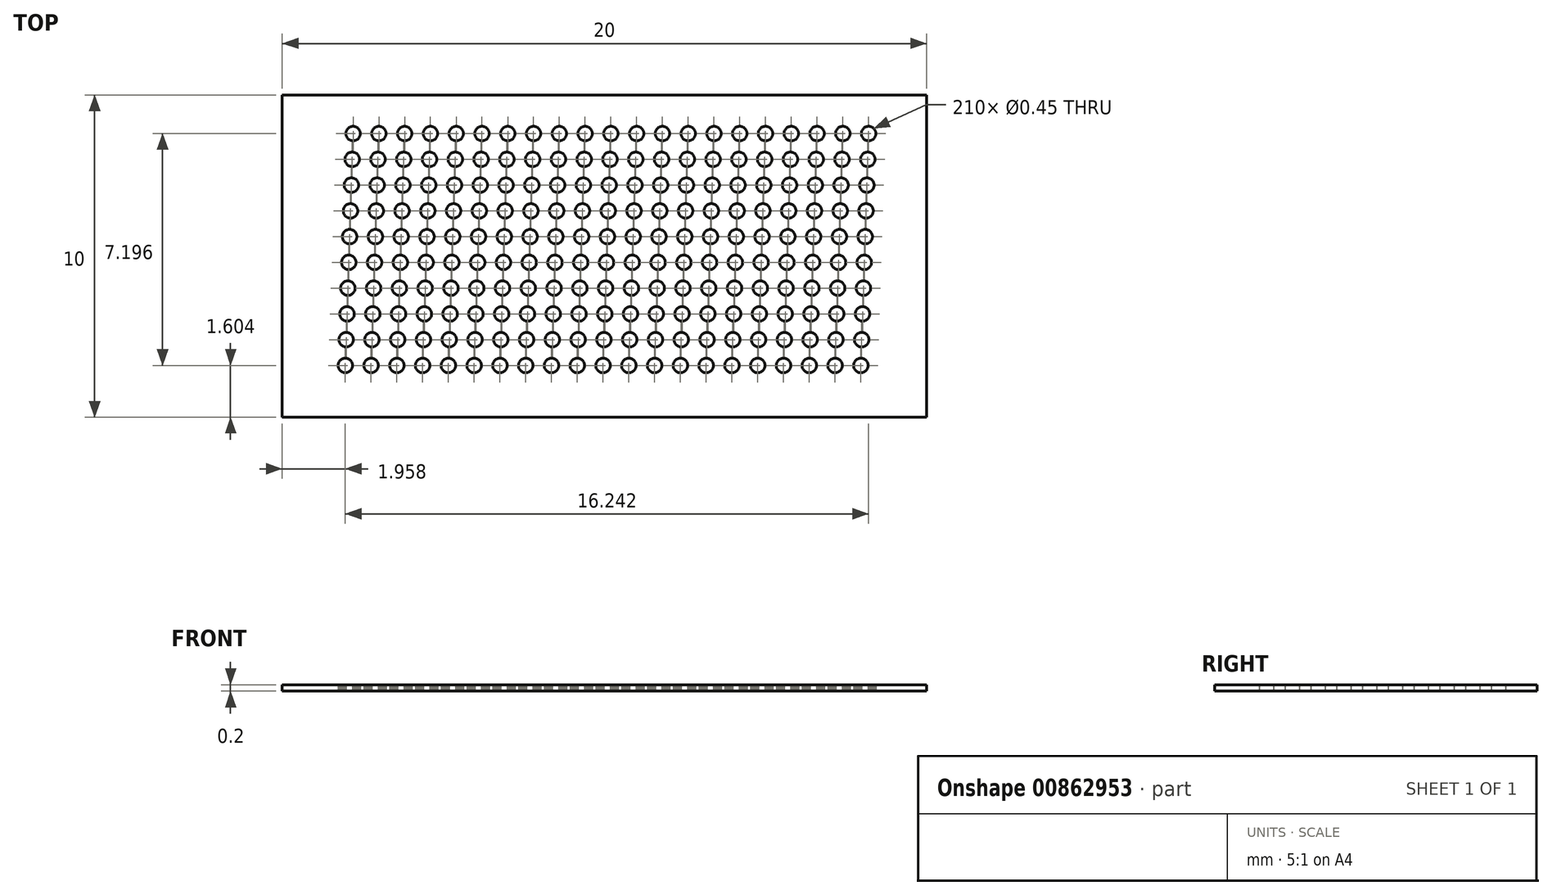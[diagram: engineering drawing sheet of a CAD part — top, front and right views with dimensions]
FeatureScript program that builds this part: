
annotation { "Feature Type Name" : "Feature", "Feature Type Description" : "" }
export const myFeature = defineFeature(function(context is Context, id is Id, definition is map)
    precondition{}
    {
        {
            var Q0;
            Q0=qCreatedBy(makeId("Top.planeOp"),FACE);
            var sketch = newSketch(context, id + "F0", { "sketchPlane" : qUnion([Q0])});
            skLineSegment(sketch, "E0.bottom", {"start": v(0, 0) * mm, "end": v(20, 0) * mm});
            skLineSegment(sketch, "E0.top", {"start": v(0, -10) * mm, "end": v(20, -10) * mm});
            skLineSegment(sketch, "E0.left", {"start": v(0, 0) * mm, "end": v(0, -10) * mm});
            skLineSegment(sketch, "E0.right", {"start": v(20, 0) * mm, "end": v(20, -10) * mm});
            skEllipse(sketch, "E1", {"center": v(2.2, -1.2) * mm, "majorRadius": 0.23 * mm, "minorRadius": 0.23 * mm, "majorAxis": v(0.92, 0.38)});
            skEllipse(sketch, "E2.1.0.0", {"center": v(3, -1.2) * mm, "majorRadius": 0.23 * mm, "minorRadius": 0.23 * mm, "majorAxis": v(0.92, 0.38)});
            skEllipse(sketch, "E2.2.0.0", {"center": v(3.8, -1.2) * mm, "majorRadius": 0.23 * mm, "minorRadius": 0.23 * mm, "majorAxis": v(0.92, 0.38)});
            skLineSegment(sketch, "E2.direction1", {"start": v(2.2, -1.2) * mm, "end": v(3, -1.2) * mm, "construction": true});
            skEllipse(sketch, "E3.0.3.0", {"center": v(4.6, -1.2) * mm, "majorRadius": 0.23 * mm, "minorRadius": 0.23 * mm, "majorAxis": v(0.92, 0.38)});
            skEllipse(sketch, "E3.0.4.0", {"center": v(5.4, -1.2) * mm, "majorRadius": 0.23 * mm, "minorRadius": 0.23 * mm, "majorAxis": v(0.92, 0.38)});
            skEllipse(sketch, "E3.0.5.0", {"center": v(6.2, -1.2) * mm, "majorRadius": 0.23 * mm, "minorRadius": 0.23 * mm, "majorAxis": v(0.92, 0.38)});
            skEllipse(sketch, "E3.0.6.0", {"center": v(7, -1.2) * mm, "majorRadius": 0.23 * mm, "minorRadius": 0.23 * mm, "majorAxis": v(0.92, 0.38)});
            skEllipse(sketch, "E3.0.7.0", {"center": v(7.8, -1.2) * mm, "majorRadius": 0.23 * mm, "minorRadius": 0.23 * mm, "majorAxis": v(0.92, 0.38)});
            skEllipse(sketch, "E3.0.8.0", {"center": v(8.6, -1.2) * mm, "majorRadius": 0.23 * mm, "minorRadius": 0.23 * mm, "majorAxis": v(0.92, 0.38)});
            skEllipse(sketch, "E3.0.9.0", {"center": v(9.4, -1.2) * mm, "majorRadius": 0.23 * mm, "minorRadius": 0.23 * mm, "majorAxis": v(0.92, 0.38)});
            skEllipse(sketch, "E3.0.10.0", {"center": v(10.2, -1.2) * mm, "majorRadius": 0.23 * mm, "minorRadius": 0.23 * mm, "majorAxis": v(0.92, 0.38)});
            skEllipse(sketch, "E3.0.11.0", {"center": v(11, -1.2) * mm, "majorRadius": 0.23 * mm, "minorRadius": 0.23 * mm, "majorAxis": v(0.92, 0.38)});
            skEllipse(sketch, "E3.0.12.0", {"center": v(11.8, -1.2) * mm, "majorRadius": 0.23 * mm, "minorRadius": 0.23 * mm, "majorAxis": v(0.92, 0.38)});
            skEllipse(sketch, "E3.0.13.0", {"center": v(12.6, -1.2) * mm, "majorRadius": 0.23 * mm, "minorRadius": 0.23 * mm, "majorAxis": v(0.92, 0.38)});
            skEllipse(sketch, "E3.0.14.0", {"center": v(13.4, -1.2) * mm, "majorRadius": 0.23 * mm, "minorRadius": 0.23 * mm, "majorAxis": v(0.92, 0.38)});
            skEllipse(sketch, "E3.0.15.0", {"center": v(14.2, -1.2) * mm, "majorRadius": 0.23 * mm, "minorRadius": 0.23 * mm, "majorAxis": v(0.92, 0.38)});
            skEllipse(sketch, "E3.0.16.0", {"center": v(15, -1.2) * mm, "majorRadius": 0.23 * mm, "minorRadius": 0.23 * mm, "majorAxis": v(0.92, 0.38)});
            skEllipse(sketch, "E3.0.17.0", {"center": v(15.8, -1.2) * mm, "majorRadius": 0.23 * mm, "minorRadius": 0.23 * mm, "majorAxis": v(0.92, 0.38)});
            skEllipse(sketch, "E3.0.18.0", {"center": v(16.6, -1.2) * mm, "majorRadius": 0.23 * mm, "minorRadius": 0.23 * mm, "majorAxis": v(0.92, 0.38)});
            skEllipse(sketch, "E3.0.19.0", {"center": v(17.4, -1.2) * mm, "majorRadius": 0.23 * mm, "minorRadius": 0.23 * mm, "majorAxis": v(0.92, 0.38)});
            skEllipse(sketch, "E4.0.20.0", {"center": v(18.2, -1.2) * mm, "majorRadius": 0.23 * mm, "minorRadius": 0.23 * mm, "majorAxis": v(0.92, 0.38)});
            skEllipse(sketch, "E5.1.0.0", {"center": v(18.17, -2) * mm, "majorRadius": 0.23 * mm, "minorRadius": 0.23 * mm, "majorAxis": v(0.92, 0.38)});
            skEllipse(sketch, "E5.1.0.1", {"center": v(17.37, -2) * mm, "majorRadius": 0.23 * mm, "minorRadius": 0.23 * mm, "majorAxis": v(0.92, 0.38)});
            skEllipse(sketch, "E5.1.0.2", {"center": v(16.57, -2) * mm, "majorRadius": 0.23 * mm, "minorRadius": 0.23 * mm, "majorAxis": v(0.92, 0.38)});
            skEllipse(sketch, "E5.1.0.3", {"center": v(15.77, -2) * mm, "majorRadius": 0.23 * mm, "minorRadius": 0.23 * mm, "majorAxis": v(0.92, 0.38)});
            skEllipse(sketch, "E5.1.0.4", {"center": v(14.97, -2) * mm, "majorRadius": 0.23 * mm, "minorRadius": 0.23 * mm, "majorAxis": v(0.92, 0.38)});
            skEllipse(sketch, "E5.1.0.5", {"center": v(14.17, -2) * mm, "majorRadius": 0.23 * mm, "minorRadius": 0.23 * mm, "majorAxis": v(0.92, 0.38)});
            skEllipse(sketch, "E5.1.0.6", {"center": v(13.37, -2) * mm, "majorRadius": 0.23 * mm, "minorRadius": 0.23 * mm, "majorAxis": v(0.92, 0.38)});
            skEllipse(sketch, "E5.1.0.7", {"center": v(12.57, -2) * mm, "majorRadius": 0.23 * mm, "minorRadius": 0.23 * mm, "majorAxis": v(0.92, 0.38)});
            skEllipse(sketch, "E5.1.0.8", {"center": v(11.77, -2) * mm, "majorRadius": 0.23 * mm, "minorRadius": 0.23 * mm, "majorAxis": v(0.92, 0.38)});
            skEllipse(sketch, "E5.1.0.9", {"center": v(10.97, -2) * mm, "majorRadius": 0.23 * mm, "minorRadius": 0.23 * mm, "majorAxis": v(0.92, 0.38)});
            skEllipse(sketch, "E5.1.0.10", {"center": v(10.17, -2) * mm, "majorRadius": 0.23 * mm, "minorRadius": 0.23 * mm, "majorAxis": v(0.92, 0.38)});
            skEllipse(sketch, "E5.1.0.11", {"center": v(9.37, -2) * mm, "majorRadius": 0.23 * mm, "minorRadius": 0.23 * mm, "majorAxis": v(0.92, 0.38)});
            skEllipse(sketch, "E5.1.0.12", {"center": v(8.57, -2) * mm, "majorRadius": 0.23 * mm, "minorRadius": 0.23 * mm, "majorAxis": v(0.92, 0.38)});
            skEllipse(sketch, "E5.1.0.13", {"center": v(7.77, -2) * mm, "majorRadius": 0.23 * mm, "minorRadius": 0.23 * mm, "majorAxis": v(0.92, 0.38)});
            skEllipse(sketch, "E5.1.0.14", {"center": v(6.97, -2) * mm, "majorRadius": 0.23 * mm, "minorRadius": 0.23 * mm, "majorAxis": v(0.92, 0.38)});
            skEllipse(sketch, "E5.1.0.15", {"center": v(5.37, -2) * mm, "majorRadius": 0.23 * mm, "minorRadius": 0.23 * mm, "majorAxis": v(0.92, 0.38)});
            skEllipse(sketch, "E5.1.0.16", {"center": v(4.57, -2) * mm, "majorRadius": 0.23 * mm, "minorRadius": 0.23 * mm, "majorAxis": v(0.92, 0.38)});
            skEllipse(sketch, "E5.1.0.17", {"center": v(6.17, -2) * mm, "majorRadius": 0.23 * mm, "minorRadius": 0.23 * mm, "majorAxis": v(0.92, 0.38)});
            skEllipse(sketch, "E5.1.0.18", {"center": v(3.77, -2) * mm, "majorRadius": 0.23 * mm, "minorRadius": 0.23 * mm, "majorAxis": v(0.92, 0.38)});
            skEllipse(sketch, "E5.1.0.19", {"center": v(2.97, -2) * mm, "majorRadius": 0.23 * mm, "minorRadius": 0.23 * mm, "majorAxis": v(0.92, 0.38)});
            skEllipse(sketch, "E5.1.0.20", {"center": v(2.17, -2) * mm, "majorRadius": 0.23 * mm, "minorRadius": 0.23 * mm, "majorAxis": v(0.92, 0.38)});
            skEllipse(sketch, "E5.2.0.0", {"center": v(18.15, -2.8) * mm, "majorRadius": 0.23 * mm, "minorRadius": 0.23 * mm, "majorAxis": v(0.92, 0.38)});
            skEllipse(sketch, "E5.2.0.1", {"center": v(17.35, -2.8) * mm, "majorRadius": 0.23 * mm, "minorRadius": 0.23 * mm, "majorAxis": v(0.92, 0.38)});
            skEllipse(sketch, "E5.2.0.2", {"center": v(16.55, -2.8) * mm, "majorRadius": 0.23 * mm, "minorRadius": 0.23 * mm, "majorAxis": v(0.92, 0.38)});
            skEllipse(sketch, "E5.2.0.3", {"center": v(15.75, -2.8) * mm, "majorRadius": 0.23 * mm, "minorRadius": 0.23 * mm, "majorAxis": v(0.92, 0.38)});
            skEllipse(sketch, "E5.2.0.4", {"center": v(14.95, -2.8) * mm, "majorRadius": 0.23 * mm, "minorRadius": 0.23 * mm, "majorAxis": v(0.92, 0.38)});
            skEllipse(sketch, "E5.2.0.5", {"center": v(14.15, -2.8) * mm, "majorRadius": 0.23 * mm, "minorRadius": 0.23 * mm, "majorAxis": v(0.92, 0.38)});
            skEllipse(sketch, "E5.2.0.6", {"center": v(13.35, -2.8) * mm, "majorRadius": 0.23 * mm, "minorRadius": 0.23 * mm, "majorAxis": v(0.92, 0.38)});
            skEllipse(sketch, "E5.2.0.7", {"center": v(12.55, -2.8) * mm, "majorRadius": 0.23 * mm, "minorRadius": 0.23 * mm, "majorAxis": v(0.92, 0.38)});
            skEllipse(sketch, "E5.2.0.8", {"center": v(11.75, -2.8) * mm, "majorRadius": 0.23 * mm, "minorRadius": 0.23 * mm, "majorAxis": v(0.92, 0.38)});
            skEllipse(sketch, "E5.2.0.9", {"center": v(10.95, -2.8) * mm, "majorRadius": 0.23 * mm, "minorRadius": 0.23 * mm, "majorAxis": v(0.92, 0.38)});
            skEllipse(sketch, "E5.2.0.10", {"center": v(10.15, -2.8) * mm, "majorRadius": 0.23 * mm, "minorRadius": 0.23 * mm, "majorAxis": v(0.92, 0.38)});
            skEllipse(sketch, "E5.2.0.11", {"center": v(9.35, -2.8) * mm, "majorRadius": 0.23 * mm, "minorRadius": 0.23 * mm, "majorAxis": v(0.92, 0.38)});
            skEllipse(sketch, "E5.2.0.12", {"center": v(8.55, -2.8) * mm, "majorRadius": 0.23 * mm, "minorRadius": 0.23 * mm, "majorAxis": v(0.92, 0.38)});
            skEllipse(sketch, "E5.2.0.13", {"center": v(7.75, -2.8) * mm, "majorRadius": 0.23 * mm, "minorRadius": 0.23 * mm, "majorAxis": v(0.92, 0.38)});
            skEllipse(sketch, "E5.2.0.14", {"center": v(6.95, -2.8) * mm, "majorRadius": 0.23 * mm, "minorRadius": 0.23 * mm, "majorAxis": v(0.92, 0.38)});
            skEllipse(sketch, "E5.2.0.15", {"center": v(5.35, -2.8) * mm, "majorRadius": 0.23 * mm, "minorRadius": 0.23 * mm, "majorAxis": v(0.92, 0.38)});
            skEllipse(sketch, "E5.2.0.16", {"center": v(4.55, -2.8) * mm, "majorRadius": 0.23 * mm, "minorRadius": 0.23 * mm, "majorAxis": v(0.92, 0.38)});
            skEllipse(sketch, "E5.2.0.17", {"center": v(6.15, -2.8) * mm, "majorRadius": 0.23 * mm, "minorRadius": 0.23 * mm, "majorAxis": v(0.92, 0.38)});
            skEllipse(sketch, "E5.2.0.18", {"center": v(3.75, -2.8) * mm, "majorRadius": 0.23 * mm, "minorRadius": 0.23 * mm, "majorAxis": v(0.92, 0.38)});
            skEllipse(sketch, "E5.2.0.19", {"center": v(2.95, -2.8) * mm, "majorRadius": 0.23 * mm, "minorRadius": 0.23 * mm, "majorAxis": v(0.92, 0.38)});
            skEllipse(sketch, "E5.2.0.20", {"center": v(2.15, -2.8) * mm, "majorRadius": 0.23 * mm, "minorRadius": 0.23 * mm, "majorAxis": v(0.92, 0.38)});
            skEllipse(sketch, "E5.3.0.0", {"center": v(18.12, -3.6) * mm, "majorRadius": 0.23 * mm, "minorRadius": 0.23 * mm, "majorAxis": v(0.92, 0.38)});
            skEllipse(sketch, "E5.3.0.1", {"center": v(17.32, -3.6) * mm, "majorRadius": 0.23 * mm, "minorRadius": 0.23 * mm, "majorAxis": v(0.92, 0.38)});
            skEllipse(sketch, "E5.3.0.2", {"center": v(16.52, -3.6) * mm, "majorRadius": 0.23 * mm, "minorRadius": 0.23 * mm, "majorAxis": v(0.92, 0.38)});
            skEllipse(sketch, "E5.3.0.3", {"center": v(15.72, -3.6) * mm, "majorRadius": 0.23 * mm, "minorRadius": 0.23 * mm, "majorAxis": v(0.92, 0.38)});
            skEllipse(sketch, "E5.3.0.4", {"center": v(14.92, -3.6) * mm, "majorRadius": 0.23 * mm, "minorRadius": 0.23 * mm, "majorAxis": v(0.92, 0.38)});
            skEllipse(sketch, "E5.3.0.5", {"center": v(14.12, -3.6) * mm, "majorRadius": 0.23 * mm, "minorRadius": 0.23 * mm, "majorAxis": v(0.92, 0.38)});
            skEllipse(sketch, "E5.3.0.6", {"center": v(13.32, -3.6) * mm, "majorRadius": 0.23 * mm, "minorRadius": 0.23 * mm, "majorAxis": v(0.92, 0.38)});
            skEllipse(sketch, "E5.3.0.7", {"center": v(12.52, -3.6) * mm, "majorRadius": 0.23 * mm, "minorRadius": 0.23 * mm, "majorAxis": v(0.92, 0.38)});
            skEllipse(sketch, "E5.3.0.8", {"center": v(11.72, -3.6) * mm, "majorRadius": 0.23 * mm, "minorRadius": 0.23 * mm, "majorAxis": v(0.92, 0.38)});
            skEllipse(sketch, "E5.3.0.9", {"center": v(10.92, -3.6) * mm, "majorRadius": 0.23 * mm, "minorRadius": 0.23 * mm, "majorAxis": v(0.92, 0.38)});
            skEllipse(sketch, "E5.3.0.10", {"center": v(10.12, -3.6) * mm, "majorRadius": 0.23 * mm, "minorRadius": 0.23 * mm, "majorAxis": v(0.92, 0.38)});
            skEllipse(sketch, "E5.3.0.11", {"center": v(9.32, -3.6) * mm, "majorRadius": 0.23 * mm, "minorRadius": 0.23 * mm, "majorAxis": v(0.92, 0.38)});
            skEllipse(sketch, "E5.3.0.12", {"center": v(8.52, -3.6) * mm, "majorRadius": 0.23 * mm, "minorRadius": 0.23 * mm, "majorAxis": v(0.92, 0.38)});
            skEllipse(sketch, "E5.3.0.13", {"center": v(7.72, -3.6) * mm, "majorRadius": 0.23 * mm, "minorRadius": 0.23 * mm, "majorAxis": v(0.92, 0.38)});
            skEllipse(sketch, "E5.3.0.14", {"center": v(6.92, -3.6) * mm, "majorRadius": 0.23 * mm, "minorRadius": 0.23 * mm, "majorAxis": v(0.92, 0.38)});
            skEllipse(sketch, "E5.3.0.15", {"center": v(5.32, -3.6) * mm, "majorRadius": 0.23 * mm, "minorRadius": 0.23 * mm, "majorAxis": v(0.92, 0.38)});
            skEllipse(sketch, "E5.3.0.16", {"center": v(4.52, -3.6) * mm, "majorRadius": 0.23 * mm, "minorRadius": 0.23 * mm, "majorAxis": v(0.92, 0.38)});
            skEllipse(sketch, "E5.3.0.17", {"center": v(6.12, -3.6) * mm, "majorRadius": 0.23 * mm, "minorRadius": 0.23 * mm, "majorAxis": v(0.92, 0.38)});
            skEllipse(sketch, "E5.3.0.18", {"center": v(3.72, -3.6) * mm, "majorRadius": 0.23 * mm, "minorRadius": 0.23 * mm, "majorAxis": v(0.92, 0.38)});
            skEllipse(sketch, "E5.3.0.19", {"center": v(2.92, -3.6) * mm, "majorRadius": 0.23 * mm, "minorRadius": 0.23 * mm, "majorAxis": v(0.92, 0.38)});
            skEllipse(sketch, "E5.3.0.20", {"center": v(2.12, -3.6) * mm, "majorRadius": 0.23 * mm, "minorRadius": 0.23 * mm, "majorAxis": v(0.92, 0.38)});
            skEllipse(sketch, "E5.4.0.0", {"center": v(18.1, -4.4) * mm, "majorRadius": 0.23 * mm, "minorRadius": 0.23 * mm, "majorAxis": v(0.92, 0.38)});
            skEllipse(sketch, "E5.4.0.1", {"center": v(17.3, -4.4) * mm, "majorRadius": 0.23 * mm, "minorRadius": 0.23 * mm, "majorAxis": v(0.92, 0.38)});
            skEllipse(sketch, "E5.4.0.2", {"center": v(16.5, -4.4) * mm, "majorRadius": 0.23 * mm, "minorRadius": 0.23 * mm, "majorAxis": v(0.92, 0.38)});
            skEllipse(sketch, "E5.4.0.3", {"center": v(15.7, -4.4) * mm, "majorRadius": 0.23 * mm, "minorRadius": 0.23 * mm, "majorAxis": v(0.92, 0.38)});
            skEllipse(sketch, "E5.4.0.4", {"center": v(14.9, -4.4) * mm, "majorRadius": 0.23 * mm, "minorRadius": 0.23 * mm, "majorAxis": v(0.92, 0.38)});
            skEllipse(sketch, "E5.4.0.5", {"center": v(14.1, -4.4) * mm, "majorRadius": 0.23 * mm, "minorRadius": 0.23 * mm, "majorAxis": v(0.92, 0.38)});
            skEllipse(sketch, "E5.4.0.6", {"center": v(13.3, -4.4) * mm, "majorRadius": 0.23 * mm, "minorRadius": 0.23 * mm, "majorAxis": v(0.92, 0.38)});
            skEllipse(sketch, "E5.4.0.7", {"center": v(12.5, -4.4) * mm, "majorRadius": 0.23 * mm, "minorRadius": 0.23 * mm, "majorAxis": v(0.92, 0.38)});
            skEllipse(sketch, "E5.4.0.8", {"center": v(11.7, -4.4) * mm, "majorRadius": 0.23 * mm, "minorRadius": 0.23 * mm, "majorAxis": v(0.92, 0.38)});
            skEllipse(sketch, "E5.4.0.9", {"center": v(10.9, -4.4) * mm, "majorRadius": 0.23 * mm, "minorRadius": 0.23 * mm, "majorAxis": v(0.92, 0.38)});
            skEllipse(sketch, "E5.4.0.10", {"center": v(10.1, -4.4) * mm, "majorRadius": 0.23 * mm, "minorRadius": 0.23 * mm, "majorAxis": v(0.92, 0.38)});
            skEllipse(sketch, "E5.4.0.11", {"center": v(9.3, -4.4) * mm, "majorRadius": 0.23 * mm, "minorRadius": 0.23 * mm, "majorAxis": v(0.92, 0.38)});
            skEllipse(sketch, "E5.4.0.12", {"center": v(8.5, -4.4) * mm, "majorRadius": 0.23 * mm, "minorRadius": 0.23 * mm, "majorAxis": v(0.92, 0.38)});
            skEllipse(sketch, "E5.4.0.13", {"center": v(7.7, -4.4) * mm, "majorRadius": 0.23 * mm, "minorRadius": 0.23 * mm, "majorAxis": v(0.92, 0.38)});
            skEllipse(sketch, "E5.4.0.14", {"center": v(6.9, -4.4) * mm, "majorRadius": 0.23 * mm, "minorRadius": 0.23 * mm, "majorAxis": v(0.92, 0.38)});
            skEllipse(sketch, "E5.4.0.15", {"center": v(5.3, -4.4) * mm, "majorRadius": 0.23 * mm, "minorRadius": 0.23 * mm, "majorAxis": v(0.92, 0.38)});
            skEllipse(sketch, "E5.4.0.16", {"center": v(4.5, -4.4) * mm, "majorRadius": 0.23 * mm, "minorRadius": 0.23 * mm, "majorAxis": v(0.92, 0.38)});
            skEllipse(sketch, "E5.4.0.17", {"center": v(6.1, -4.4) * mm, "majorRadius": 0.23 * mm, "minorRadius": 0.23 * mm, "majorAxis": v(0.92, 0.38)});
            skEllipse(sketch, "E5.4.0.18", {"center": v(3.7, -4.4) * mm, "majorRadius": 0.23 * mm, "minorRadius": 0.23 * mm, "majorAxis": v(0.92, 0.38)});
            skEllipse(sketch, "E5.4.0.19", {"center": v(2.9, -4.4) * mm, "majorRadius": 0.23 * mm, "minorRadius": 0.23 * mm, "majorAxis": v(0.92, 0.38)});
            skEllipse(sketch, "E5.4.0.20", {"center": v(2.1, -4.4) * mm, "majorRadius": 0.23 * mm, "minorRadius": 0.23 * mm, "majorAxis": v(0.92, 0.38)});
            skEllipse(sketch, "E5.5.0.0", {"center": v(18.07, -5.2) * mm, "majorRadius": 0.23 * mm, "minorRadius": 0.23 * mm, "majorAxis": v(0.92, 0.38)});
            skEllipse(sketch, "E5.5.0.1", {"center": v(17.27, -5.2) * mm, "majorRadius": 0.23 * mm, "minorRadius": 0.23 * mm, "majorAxis": v(0.92, 0.38)});
            skEllipse(sketch, "E5.5.0.2", {"center": v(16.47, -5.2) * mm, "majorRadius": 0.23 * mm, "minorRadius": 0.23 * mm, "majorAxis": v(0.92, 0.38)});
            skEllipse(sketch, "E5.5.0.3", {"center": v(15.67, -5.2) * mm, "majorRadius": 0.23 * mm, "minorRadius": 0.23 * mm, "majorAxis": v(0.92, 0.38)});
            skEllipse(sketch, "E5.5.0.4", {"center": v(14.87, -5.2) * mm, "majorRadius": 0.23 * mm, "minorRadius": 0.23 * mm, "majorAxis": v(0.92, 0.38)});
            skEllipse(sketch, "E5.5.0.5", {"center": v(14.07, -5.2) * mm, "majorRadius": 0.23 * mm, "minorRadius": 0.23 * mm, "majorAxis": v(0.92, 0.38)});
            skEllipse(sketch, "E5.5.0.6", {"center": v(13.27, -5.2) * mm, "majorRadius": 0.23 * mm, "minorRadius": 0.23 * mm, "majorAxis": v(0.92, 0.38)});
            skEllipse(sketch, "E5.5.0.7", {"center": v(12.47, -5.2) * mm, "majorRadius": 0.23 * mm, "minorRadius": 0.23 * mm, "majorAxis": v(0.92, 0.38)});
            skEllipse(sketch, "E5.5.0.8", {"center": v(11.67, -5.2) * mm, "majorRadius": 0.23 * mm, "minorRadius": 0.23 * mm, "majorAxis": v(0.92, 0.38)});
            skEllipse(sketch, "E5.5.0.9", {"center": v(10.87, -5.2) * mm, "majorRadius": 0.23 * mm, "minorRadius": 0.23 * mm, "majorAxis": v(0.92, 0.38)});
            skEllipse(sketch, "E5.5.0.10", {"center": v(10.07, -5.2) * mm, "majorRadius": 0.23 * mm, "minorRadius": 0.23 * mm, "majorAxis": v(0.92, 0.38)});
            skEllipse(sketch, "E5.5.0.11", {"center": v(9.27, -5.2) * mm, "majorRadius": 0.23 * mm, "minorRadius": 0.23 * mm, "majorAxis": v(0.92, 0.38)});
            skEllipse(sketch, "E5.5.0.12", {"center": v(8.47, -5.2) * mm, "majorRadius": 0.23 * mm, "minorRadius": 0.23 * mm, "majorAxis": v(0.92, 0.38)});
            skEllipse(sketch, "E5.5.0.13", {"center": v(7.67, -5.2) * mm, "majorRadius": 0.23 * mm, "minorRadius": 0.23 * mm, "majorAxis": v(0.92, 0.38)});
            skEllipse(sketch, "E5.5.0.14", {"center": v(6.87, -5.2) * mm, "majorRadius": 0.23 * mm, "minorRadius": 0.23 * mm, "majorAxis": v(0.92, 0.38)});
            skEllipse(sketch, "E5.5.0.15", {"center": v(5.27, -5.2) * mm, "majorRadius": 0.23 * mm, "minorRadius": 0.23 * mm, "majorAxis": v(0.92, 0.38)});
            skEllipse(sketch, "E5.5.0.16", {"center": v(4.47, -5.2) * mm, "majorRadius": 0.23 * mm, "minorRadius": 0.23 * mm, "majorAxis": v(0.92, 0.38)});
            skEllipse(sketch, "E5.5.0.17", {"center": v(6.07, -5.2) * mm, "majorRadius": 0.23 * mm, "minorRadius": 0.23 * mm, "majorAxis": v(0.92, 0.38)});
            skEllipse(sketch, "E5.5.0.18", {"center": v(3.67, -5.2) * mm, "majorRadius": 0.23 * mm, "minorRadius": 0.23 * mm, "majorAxis": v(0.92, 0.38)});
            skEllipse(sketch, "E5.5.0.19", {"center": v(2.87, -5.2) * mm, "majorRadius": 0.23 * mm, "minorRadius": 0.23 * mm, "majorAxis": v(0.92, 0.38)});
            skEllipse(sketch, "E5.5.0.20", {"center": v(2.07, -5.2) * mm, "majorRadius": 0.23 * mm, "minorRadius": 0.23 * mm, "majorAxis": v(0.92, 0.38)});
            skEllipse(sketch, "E5.6.0.0", {"center": v(18.04, -6) * mm, "majorRadius": 0.23 * mm, "minorRadius": 0.23 * mm, "majorAxis": v(0.92, 0.38)});
            skEllipse(sketch, "E5.6.0.1", {"center": v(17.24, -6) * mm, "majorRadius": 0.23 * mm, "minorRadius": 0.23 * mm, "majorAxis": v(0.92, 0.38)});
            skEllipse(sketch, "E5.6.0.2", {"center": v(16.44, -6) * mm, "majorRadius": 0.23 * mm, "minorRadius": 0.23 * mm, "majorAxis": v(0.92, 0.38)});
            skEllipse(sketch, "E5.6.0.3", {"center": v(15.64, -6) * mm, "majorRadius": 0.23 * mm, "minorRadius": 0.23 * mm, "majorAxis": v(0.92, 0.38)});
            skEllipse(sketch, "E5.6.0.4", {"center": v(14.84, -6) * mm, "majorRadius": 0.23 * mm, "minorRadius": 0.23 * mm, "majorAxis": v(0.92, 0.38)});
            skEllipse(sketch, "E5.6.0.5", {"center": v(14.04, -6) * mm, "majorRadius": 0.23 * mm, "minorRadius": 0.23 * mm, "majorAxis": v(0.92, 0.38)});
            skEllipse(sketch, "E5.6.0.6", {"center": v(13.24, -6) * mm, "majorRadius": 0.23 * mm, "minorRadius": 0.23 * mm, "majorAxis": v(0.92, 0.38)});
            skEllipse(sketch, "E5.6.0.7", {"center": v(12.44, -6) * mm, "majorRadius": 0.23 * mm, "minorRadius": 0.23 * mm, "majorAxis": v(0.92, 0.38)});
            skEllipse(sketch, "E5.6.0.8", {"center": v(11.64, -6) * mm, "majorRadius": 0.23 * mm, "minorRadius": 0.23 * mm, "majorAxis": v(0.92, 0.38)});
            skEllipse(sketch, "E5.6.0.9", {"center": v(10.84, -6) * mm, "majorRadius": 0.23 * mm, "minorRadius": 0.23 * mm, "majorAxis": v(0.92, 0.38)});
            skEllipse(sketch, "E5.6.0.10", {"center": v(10.04, -6) * mm, "majorRadius": 0.23 * mm, "minorRadius": 0.23 * mm, "majorAxis": v(0.92, 0.38)});
            skEllipse(sketch, "E5.6.0.11", {"center": v(9.24, -6) * mm, "majorRadius": 0.23 * mm, "minorRadius": 0.23 * mm, "majorAxis": v(0.92, 0.38)});
            skEllipse(sketch, "E5.6.0.12", {"center": v(8.44, -6) * mm, "majorRadius": 0.23 * mm, "minorRadius": 0.23 * mm, "majorAxis": v(0.92, 0.38)});
            skEllipse(sketch, "E5.6.0.13", {"center": v(7.64, -6) * mm, "majorRadius": 0.23 * mm, "minorRadius": 0.23 * mm, "majorAxis": v(0.92, 0.38)});
            skEllipse(sketch, "E5.6.0.14", {"center": v(6.84, -6) * mm, "majorRadius": 0.23 * mm, "minorRadius": 0.23 * mm, "majorAxis": v(0.92, 0.38)});
            skEllipse(sketch, "E5.6.0.15", {"center": v(5.24, -6) * mm, "majorRadius": 0.23 * mm, "minorRadius": 0.23 * mm, "majorAxis": v(0.92, 0.38)});
            skEllipse(sketch, "E5.6.0.16", {"center": v(4.44, -6) * mm, "majorRadius": 0.23 * mm, "minorRadius": 0.23 * mm, "majorAxis": v(0.92, 0.38)});
            skEllipse(sketch, "E5.6.0.17", {"center": v(6.04, -6) * mm, "majorRadius": 0.23 * mm, "minorRadius": 0.23 * mm, "majorAxis": v(0.92, 0.38)});
            skEllipse(sketch, "E5.6.0.18", {"center": v(3.64, -6) * mm, "majorRadius": 0.23 * mm, "minorRadius": 0.23 * mm, "majorAxis": v(0.92, 0.38)});
            skEllipse(sketch, "E5.6.0.19", {"center": v(2.84, -6) * mm, "majorRadius": 0.23 * mm, "minorRadius": 0.23 * mm, "majorAxis": v(0.92, 0.38)});
            skEllipse(sketch, "E5.6.0.20", {"center": v(2.04, -6) * mm, "majorRadius": 0.23 * mm, "minorRadius": 0.23 * mm, "majorAxis": v(0.92, 0.38)});
            skEllipse(sketch, "E5.7.0.0", {"center": v(18.01, -6.8) * mm, "majorRadius": 0.23 * mm, "minorRadius": 0.23 * mm, "majorAxis": v(0.92, 0.38)});
            skEllipse(sketch, "E5.7.0.1", {"center": v(17.21, -6.8) * mm, "majorRadius": 0.23 * mm, "minorRadius": 0.23 * mm, "majorAxis": v(0.92, 0.38)});
            skEllipse(sketch, "E5.7.0.2", {"center": v(16.41, -6.8) * mm, "majorRadius": 0.23 * mm, "minorRadius": 0.23 * mm, "majorAxis": v(0.92, 0.38)});
            skEllipse(sketch, "E5.7.0.3", {"center": v(15.61, -6.8) * mm, "majorRadius": 0.23 * mm, "minorRadius": 0.23 * mm, "majorAxis": v(0.92, 0.38)});
            skEllipse(sketch, "E5.7.0.4", {"center": v(14.81, -6.8) * mm, "majorRadius": 0.23 * mm, "minorRadius": 0.23 * mm, "majorAxis": v(0.92, 0.38)});
            skEllipse(sketch, "E5.7.0.5", {"center": v(14.01, -6.8) * mm, "majorRadius": 0.23 * mm, "minorRadius": 0.23 * mm, "majorAxis": v(0.92, 0.38)});
            skEllipse(sketch, "E5.7.0.6", {"center": v(13.21, -6.8) * mm, "majorRadius": 0.23 * mm, "minorRadius": 0.23 * mm, "majorAxis": v(0.92, 0.38)});
            skEllipse(sketch, "E5.7.0.7", {"center": v(12.41, -6.8) * mm, "majorRadius": 0.23 * mm, "minorRadius": 0.23 * mm, "majorAxis": v(0.92, 0.38)});
            skEllipse(sketch, "E5.7.0.8", {"center": v(11.61, -6.8) * mm, "majorRadius": 0.23 * mm, "minorRadius": 0.23 * mm, "majorAxis": v(0.92, 0.38)});
            skEllipse(sketch, "E5.7.0.9", {"center": v(10.81, -6.8) * mm, "majorRadius": 0.23 * mm, "minorRadius": 0.23 * mm, "majorAxis": v(0.92, 0.38)});
            skEllipse(sketch, "E5.7.0.10", {"center": v(10.01, -6.8) * mm, "majorRadius": 0.23 * mm, "minorRadius": 0.23 * mm, "majorAxis": v(0.92, 0.38)});
            skEllipse(sketch, "E5.7.0.11", {"center": v(9.21, -6.8) * mm, "majorRadius": 0.23 * mm, "minorRadius": 0.23 * mm, "majorAxis": v(0.92, 0.38)});
            skEllipse(sketch, "E5.7.0.12", {"center": v(8.41, -6.8) * mm, "majorRadius": 0.23 * mm, "minorRadius": 0.23 * mm, "majorAxis": v(0.92, 0.38)});
            skEllipse(sketch, "E5.7.0.13", {"center": v(7.61, -6.8) * mm, "majorRadius": 0.23 * mm, "minorRadius": 0.23 * mm, "majorAxis": v(0.92, 0.38)});
            skEllipse(sketch, "E5.7.0.14", {"center": v(6.81, -6.8) * mm, "majorRadius": 0.23 * mm, "minorRadius": 0.23 * mm, "majorAxis": v(0.92, 0.38)});
            skEllipse(sketch, "E5.7.0.15", {"center": v(5.21, -6.8) * mm, "majorRadius": 0.23 * mm, "minorRadius": 0.23 * mm, "majorAxis": v(0.92, 0.38)});
            skEllipse(sketch, "E5.7.0.16", {"center": v(4.41, -6.8) * mm, "majorRadius": 0.23 * mm, "minorRadius": 0.23 * mm, "majorAxis": v(0.92, 0.38)});
            skEllipse(sketch, "E5.7.0.17", {"center": v(6.01, -6.8) * mm, "majorRadius": 0.23 * mm, "minorRadius": 0.23 * mm, "majorAxis": v(0.92, 0.38)});
            skEllipse(sketch, "E5.7.0.18", {"center": v(3.61, -6.8) * mm, "majorRadius": 0.23 * mm, "minorRadius": 0.23 * mm, "majorAxis": v(0.92, 0.38)});
            skEllipse(sketch, "E5.7.0.19", {"center": v(2.81, -6.8) * mm, "majorRadius": 0.23 * mm, "minorRadius": 0.23 * mm, "majorAxis": v(0.92, 0.38)});
            skEllipse(sketch, "E5.7.0.20", {"center": v(2.01, -6.8) * mm, "majorRadius": 0.23 * mm, "minorRadius": 0.23 * mm, "majorAxis": v(0.92, 0.38)});
            skEllipse(sketch, "E5.8.0.0", {"center": v(17.98, -7.6) * mm, "majorRadius": 0.23 * mm, "minorRadius": 0.23 * mm, "majorAxis": v(0.92, 0.38)});
            skEllipse(sketch, "E5.8.0.1", {"center": v(17.18, -7.6) * mm, "majorRadius": 0.23 * mm, "minorRadius": 0.23 * mm, "majorAxis": v(0.92, 0.38)});
            skEllipse(sketch, "E5.8.0.2", {"center": v(16.38, -7.6) * mm, "majorRadius": 0.23 * mm, "minorRadius": 0.23 * mm, "majorAxis": v(0.92, 0.38)});
            skEllipse(sketch, "E5.8.0.3", {"center": v(15.58, -7.6) * mm, "majorRadius": 0.23 * mm, "minorRadius": 0.23 * mm, "majorAxis": v(0.92, 0.38)});
            skEllipse(sketch, "E5.8.0.4", {"center": v(14.78, -7.6) * mm, "majorRadius": 0.23 * mm, "minorRadius": 0.23 * mm, "majorAxis": v(0.92, 0.38)});
            skEllipse(sketch, "E5.8.0.5", {"center": v(13.98, -7.6) * mm, "majorRadius": 0.23 * mm, "minorRadius": 0.23 * mm, "majorAxis": v(0.92, 0.38)});
            skEllipse(sketch, "E5.8.0.6", {"center": v(13.18, -7.6) * mm, "majorRadius": 0.23 * mm, "minorRadius": 0.23 * mm, "majorAxis": v(0.92, 0.38)});
            skEllipse(sketch, "E5.8.0.7", {"center": v(12.38, -7.6) * mm, "majorRadius": 0.23 * mm, "minorRadius": 0.23 * mm, "majorAxis": v(0.92, 0.38)});
            skEllipse(sketch, "E5.8.0.8", {"center": v(11.58, -7.6) * mm, "majorRadius": 0.23 * mm, "minorRadius": 0.23 * mm, "majorAxis": v(0.92, 0.38)});
            skEllipse(sketch, "E5.8.0.9", {"center": v(10.78, -7.6) * mm, "majorRadius": 0.23 * mm, "minorRadius": 0.23 * mm, "majorAxis": v(0.92, 0.38)});
            skEllipse(sketch, "E5.8.0.10", {"center": v(9.98, -7.6) * mm, "majorRadius": 0.23 * mm, "minorRadius": 0.23 * mm, "majorAxis": v(0.92, 0.38)});
            skEllipse(sketch, "E5.8.0.11", {"center": v(9.18, -7.6) * mm, "majorRadius": 0.23 * mm, "minorRadius": 0.23 * mm, "majorAxis": v(0.92, 0.38)});
            skEllipse(sketch, "E5.8.0.12", {"center": v(8.38, -7.6) * mm, "majorRadius": 0.23 * mm, "minorRadius": 0.23 * mm, "majorAxis": v(0.92, 0.38)});
            skEllipse(sketch, "E5.8.0.13", {"center": v(7.58, -7.6) * mm, "majorRadius": 0.23 * mm, "minorRadius": 0.23 * mm, "majorAxis": v(0.92, 0.38)});
            skEllipse(sketch, "E5.8.0.14", {"center": v(6.78, -7.6) * mm, "majorRadius": 0.23 * mm, "minorRadius": 0.23 * mm, "majorAxis": v(0.92, 0.38)});
            skEllipse(sketch, "E5.8.0.15", {"center": v(5.18, -7.6) * mm, "majorRadius": 0.23 * mm, "minorRadius": 0.23 * mm, "majorAxis": v(0.92, 0.38)});
            skEllipse(sketch, "E5.8.0.16", {"center": v(4.38, -7.6) * mm, "majorRadius": 0.23 * mm, "minorRadius": 0.23 * mm, "majorAxis": v(0.92, 0.38)});
            skEllipse(sketch, "E5.8.0.17", {"center": v(5.98, -7.6) * mm, "majorRadius": 0.23 * mm, "minorRadius": 0.23 * mm, "majorAxis": v(0.92, 0.38)});
            skEllipse(sketch, "E5.8.0.18", {"center": v(3.58, -7.6) * mm, "majorRadius": 0.23 * mm, "minorRadius": 0.23 * mm, "majorAxis": v(0.92, 0.38)});
            skEllipse(sketch, "E5.8.0.19", {"center": v(2.78, -7.6) * mm, "majorRadius": 0.23 * mm, "minorRadius": 0.23 * mm, "majorAxis": v(0.92, 0.38)});
            skEllipse(sketch, "E5.8.0.20", {"center": v(1.98, -7.6) * mm, "majorRadius": 0.23 * mm, "minorRadius": 0.23 * mm, "majorAxis": v(0.92, 0.38)});
            skEllipse(sketch, "E5.9.0.0", {"center": v(17.96, -8.4) * mm, "majorRadius": 0.23 * mm, "minorRadius": 0.23 * mm, "majorAxis": v(0.92, 0.38)});
            skEllipse(sketch, "E5.9.0.1", {"center": v(17.16, -8.4) * mm, "majorRadius": 0.23 * mm, "minorRadius": 0.23 * mm, "majorAxis": v(0.92, 0.38)});
            skEllipse(sketch, "E5.9.0.2", {"center": v(16.36, -8.4) * mm, "majorRadius": 0.23 * mm, "minorRadius": 0.23 * mm, "majorAxis": v(0.92, 0.38)});
            skEllipse(sketch, "E5.9.0.3", {"center": v(15.56, -8.4) * mm, "majorRadius": 0.23 * mm, "minorRadius": 0.23 * mm, "majorAxis": v(0.92, 0.38)});
            skEllipse(sketch, "E5.9.0.4", {"center": v(14.76, -8.4) * mm, "majorRadius": 0.23 * mm, "minorRadius": 0.23 * mm, "majorAxis": v(0.92, 0.38)});
            skEllipse(sketch, "E5.9.0.5", {"center": v(13.96, -8.4) * mm, "majorRadius": 0.23 * mm, "minorRadius": 0.23 * mm, "majorAxis": v(0.92, 0.38)});
            skEllipse(sketch, "E5.9.0.6", {"center": v(13.16, -8.4) * mm, "majorRadius": 0.23 * mm, "minorRadius": 0.23 * mm, "majorAxis": v(0.92, 0.38)});
            skEllipse(sketch, "E5.9.0.7", {"center": v(12.36, -8.4) * mm, "majorRadius": 0.23 * mm, "minorRadius": 0.23 * mm, "majorAxis": v(0.92, 0.38)});
            skEllipse(sketch, "E5.9.0.8", {"center": v(11.56, -8.4) * mm, "majorRadius": 0.23 * mm, "minorRadius": 0.23 * mm, "majorAxis": v(0.92, 0.38)});
            skEllipse(sketch, "E5.9.0.9", {"center": v(10.76, -8.4) * mm, "majorRadius": 0.23 * mm, "minorRadius": 0.23 * mm, "majorAxis": v(0.92, 0.38)});
            skEllipse(sketch, "E5.9.0.10", {"center": v(9.96, -8.4) * mm, "majorRadius": 0.23 * mm, "minorRadius": 0.23 * mm, "majorAxis": v(0.92, 0.38)});
            skEllipse(sketch, "E5.9.0.11", {"center": v(9.16, -8.4) * mm, "majorRadius": 0.23 * mm, "minorRadius": 0.23 * mm, "majorAxis": v(0.92, 0.38)});
            skEllipse(sketch, "E5.9.0.12", {"center": v(8.36, -8.4) * mm, "majorRadius": 0.23 * mm, "minorRadius": 0.23 * mm, "majorAxis": v(0.92, 0.38)});
            skEllipse(sketch, "E5.9.0.13", {"center": v(7.56, -8.4) * mm, "majorRadius": 0.23 * mm, "minorRadius": 0.23 * mm, "majorAxis": v(0.92, 0.38)});
            skEllipse(sketch, "E5.9.0.14", {"center": v(6.76, -8.4) * mm, "majorRadius": 0.23 * mm, "minorRadius": 0.23 * mm, "majorAxis": v(0.92, 0.38)});
            skEllipse(sketch, "E5.9.0.15", {"center": v(5.16, -8.4) * mm, "majorRadius": 0.23 * mm, "minorRadius": 0.23 * mm, "majorAxis": v(0.92, 0.38)});
            skEllipse(sketch, "E5.9.0.16", {"center": v(4.36, -8.4) * mm, "majorRadius": 0.23 * mm, "minorRadius": 0.23 * mm, "majorAxis": v(0.92, 0.38)});
            skEllipse(sketch, "E5.9.0.17", {"center": v(5.96, -8.4) * mm, "majorRadius": 0.23 * mm, "minorRadius": 0.23 * mm, "majorAxis": v(0.92, 0.38)});
            skEllipse(sketch, "E5.9.0.18", {"center": v(3.56, -8.4) * mm, "majorRadius": 0.23 * mm, "minorRadius": 0.23 * mm, "majorAxis": v(0.92, 0.38)});
            skEllipse(sketch, "E5.9.0.19", {"center": v(2.76, -8.4) * mm, "majorRadius": 0.23 * mm, "minorRadius": 0.23 * mm, "majorAxis": v(0.92, 0.38)});
            skEllipse(sketch, "E5.9.0.20", {"center": v(1.96, -8.4) * mm, "majorRadius": 0.23 * mm, "minorRadius": 0.23 * mm, "majorAxis": v(0.92, 0.38)});
            skLineSegment(sketch, "E5.direction1", {"start": v(18.2, -1.2) * mm, "end": v(18.17, -2) * mm, "construction": true});
            skSolve(sketch);
        }
        {
            var Q0;
            Q0=makeQuery(id+"F0.imprint","IMPRINT",FACE,{"disambiguationData":[TD([[makeQuery(id+"F0.imprint","IMPRINT",EDGE,{"derivedFrom":sQuery(id+"F0.wireOp",EDGE,"E0.bottom")}),-1.0]])]});
            extrude(context, id + "F1", {"entities" : qUnion([Q0]), "depth" : 0.2 * mm, "offsetDistance" : 25.4 * mm});
        }
    });
